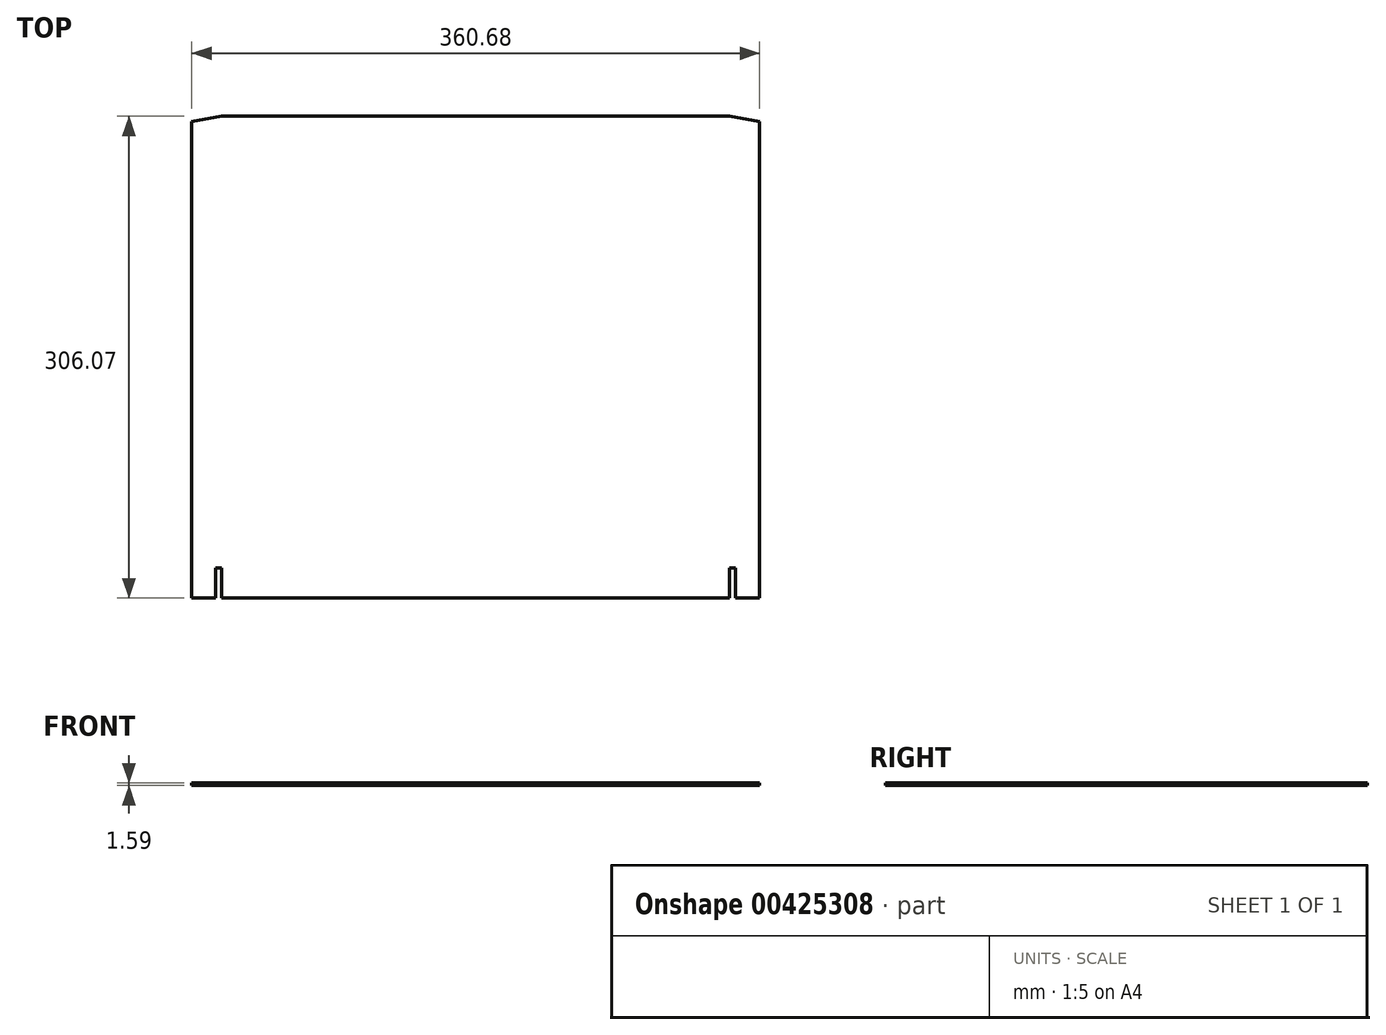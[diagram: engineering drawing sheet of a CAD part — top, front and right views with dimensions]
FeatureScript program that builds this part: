
annotation { "Feature Type Name" : "Feature", "Feature Type Description" : "" }
export const myFeature = defineFeature(function(context is Context, id is Id, definition is map)
    precondition{}
    {
        {
            var Q0;
            Q0=qCreatedBy(makeId("Top.planeOp"),FACE);
            var sketch = newSketch(context, id + "F0", { "sketchPlane" : qUnion([Q0])});
            skLineSegment(sketch, "E0.bottom", {"start": v(161.3, 143.5) * mm, "end": v(-161.3, 143.5) * mm});
            skLineSegment(sketch, "E0.top", {"start": v(161.3, -143.51) * mm, "end": v(-161.3, -143.51) * mm});
            skLineSegment(sketch, "E0.left", {"start": v(161.29, 143.51) * mm, "end": v(161.29, -143.5) * mm});
            skLineSegment(sketch, "E0.right", {"start": v(-161.3, 143.51) * mm, "end": v(-161.3, -143.5) * mm});
            skPoint(sketch, "E0.middle", {"position": v(0, 0) * mm});
            skLineSegment(sketch, "E1", {"start": v(-161.3, 143.5) * mm, "end": v(-180.34, 140.15) * mm});
            skLineSegment(sketch, "E2", {"start": v(-180.34, 140.15) * mm, "end": v(-180.34, -143.51) * mm});
            skLineSegment(sketch, "E3", {"start": v(-180.34, -143.51) * mm, "end": v(-161.3, -143.51) * mm});
            skLineSegment(sketch, "E4", {"start": v(-161.3, -143.5) * mm, "end": v(-161.3, -162.56) * mm});
            skLineSegment(sketch, "E5", {"start": v(-161.3, -162.56) * mm, "end": v(161.3, -162.56) * mm});
            skLineSegment(sketch, "E6", {"start": v(161.29, -162.56) * mm, "end": v(161.29, -143.5) * mm});
            skLineSegment(sketch, "E7", {"start": v(161.3, -143.51) * mm, "end": v(180.34, -143.51) * mm});
            skLineSegment(sketch, "E8", {"start": v(180.34, -143.51) * mm, "end": v(180.34, 140.15) * mm});
            skLineSegment(sketch, "E9", {"start": v(161.3, 143.51) * mm, "end": v(180.34, 140.15) * mm});
            skLineSegment(sketch, "E10", {"start": v(180.34, -143.51) * mm, "end": v(180.34, -162.56) * mm});
            skLineSegment(sketch, "E11", {"start": v(180.34, -162.56) * mm, "end": v(165.1, -162.56) * mm});
            skLineSegment(sketch, "E12", {"start": v(165.1, -162.56) * mm, "end": v(165.1, -143.51) * mm});
            skLineSegment(sketch, "E13", {"start": v(-180.34, -143.51) * mm, "end": v(-180.34, -162.56) * mm});
            skLineSegment(sketch, "E14", {"start": v(-180.34, -162.56) * mm, "end": v(-165.1, -162.56) * mm});
            skLineSegment(sketch, "E15", {"start": v(-165.1, -162.56) * mm, "end": v(-165.1, -143.51) * mm});
            skSolve(sketch);
        }
        {
            var Q0;
            Q0=makeQuery(id+"F0.imprint","IMPRINT",FACE,{"disambiguationData":[TD([[makeQuery(id+"F0.imprint","IMPRINT",EDGE,{"derivedFrom":sQuery(id+"F0.wireOp",EDGE,"E0.bottom")}),1.0]])]});
            var Q1;
            Q1=makeQuery(id+"F0.imprint","IMPRINT",FACE,{"disambiguationData":[TD([[makeQuery(id+"F0.imprint","IMPRINT",EDGE,{"derivedFrom":sQuery(id+"F0.wireOp",EDGE,"E0.top")}),1.0]])]});
            var Q2;
            {var subQ3=sQuery(id+"F0.wireOp",EDGE,"E0.right");Q2=makeQuery(id+"F0.imprint","IMPRINT",FACE,{"disambiguationData":[TD([[makeQuery(id+"F0.imprint","IMPRINT",EDGE,{"derivedFrom":subQ3}),-1.0]])]});}
            var Q3;
            {var subQ0=sQuery(id+"F0.wireOp",EDGE,"E13");Q3=makeQuery(id+"F0.imprint","IMPRINT",FACE,{"disambiguationData":[TD([[makeQuery(id+"F0.imprint","IMPRINT",EDGE,{"derivedFrom":subQ0}),1.0]])]});}
            var Q4;
            {var subQ0=sQuery(id+"F0.wireOp",EDGE,"E10");Q4=makeQuery(id+"F0.imprint","IMPRINT",FACE,{"disambiguationData":[TD([[makeQuery(id+"F0.imprint","IMPRINT",EDGE,{"derivedFrom":subQ0}),-1.0]])]});}
            var Q5;
            {var subQ1=sQuery(id+"F0.wireOp",EDGE,"E0.left");Q5=makeQuery(id+"F0.imprint","IMPRINT",FACE,{"disambiguationData":[TD([[makeQuery(id+"F0.imprint","IMPRINT",EDGE,{"derivedFrom":subQ1}),1.0]])]});}
            extrude(context, id + "F1", {"entities" : qUnion([Q0, Q1, Q2, Q3, Q4, Q5]), "depth" : 1.59 * mm});
        }
    });
